# Revit family: 71251SGP_NEW
name_source: partatom
category: Plumbing Fixtures
revit_build: Autodesk Revit 2018 (Build: 20170223_1515(x64)
units: mm (PartAtom-declared; Revit-internal decimal feet)

## family parameters
Always vertical = No
Cut with Voids When Loaded = No
OmniClass Number = 23.45.00.00
OmniClass Title = Sanitary, Laundry, and Cleaning Equipment
Part Type = Normal
Room Calculation Point = No
Round Connector Dimension = Use Diameter
Shared = No
Work Plane-Based = Yes

## types (1)
- 009 Chrome
    Always visible = Yes
    BIMobject category = Basins
    Default Elevation = 1219 mm
    Design country = Germany
    EAN code = 4059625356197
    Edition number = 1
    GTIN code = https://4059625356210
    IFC Classification = Sanitary Terminal
    Installation instructions = https://www.hansgrohe.com
    Manufacturer country = Germany
    Manufacturer name = hansgrohe
    Material 1 = Hansgrohe - Logis - 009 Chrome
    Material secondary = Chrome
    Product Guid = 37ca7f8e-d572-40bb-b138-44635a62853d
    Product SKU = 71251SGP
    Product data url = https://www.bimobject.com
    Product family = Logis
    Product group = Basin mixers
    Product name = 71251SGP Logis Single lever basin mixer 110 Fine with pop-up waste set 2 ticks
    Product url = https://www.hansgrohe.com
    QR code = https://www.bimobject.com
    Technical description = https://www.hansgrohe.com
    Weight Net (Kg) = 1,3

## geometry (parser evidence)
native form markers: Sweep x2
no freeform markers — native parametric forms only
